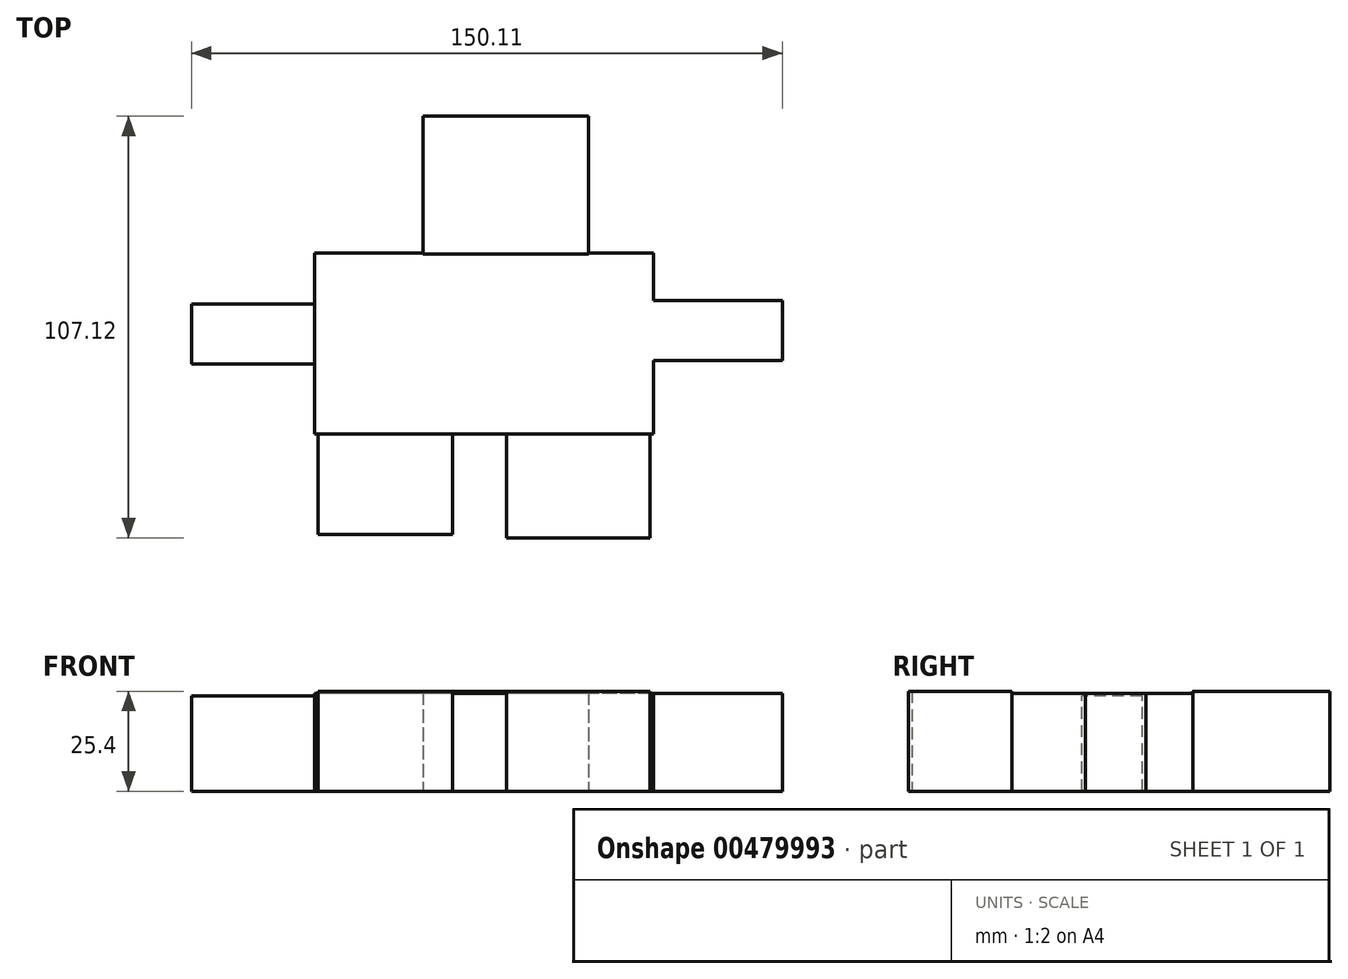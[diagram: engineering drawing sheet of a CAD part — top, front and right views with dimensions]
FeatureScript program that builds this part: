
annotation { "Feature Type Name" : "Feature", "Feature Type Description" : "" }
export const myFeature = defineFeature(function(context is Context, id is Id, definition is map)
    precondition{}
    {
        {
            var Q0;
            Q0=qCreatedBy(makeId("Top.planeOp"),FACE);
            var sketch = newSketch(context, id + "F0", { "sketchPlane" : qUnion([Q0])});
            skLineSegment(sketch, "E0.bottom", {"start": v(-55.67, -25.5) * mm, "end": v(-21.57, -25.5) * mm});
            skLineSegment(sketch, "E0.top", {"start": v(-55.67, 0) * mm, "end": v(-21.57, 0) * mm});
            skLineSegment(sketch, "E0.left", {"start": v(-55.67, -25.5) * mm, "end": v(-55.67, 0) * mm});
            skLineSegment(sketch, "E0.right", {"start": v(-21.57, -25.5) * mm, "end": v(-21.57, 0) * mm});
            skLineSegment(sketch, "E1.bottom", {"start": v(-7.87, -26.38) * mm, "end": v(28.56, -26.38) * mm});
            skLineSegment(sketch, "E1.top", {"start": v(-7.87, 0) * mm, "end": v(28.56, 0) * mm});
            skLineSegment(sketch, "E1.left", {"start": v(-7.87, -26.38) * mm, "end": v(-7.87, 0) * mm});
            skLineSegment(sketch, "E1.right", {"start": v(28.56, -26.38) * mm, "end": v(28.56, 0) * mm});
            skSolve(sketch);
        }
        {
            var Q0;
            Q0 = qSketchRegion(id + "F0", true);
            extrude(context, id + "F1", {"entities" : qUnion([Q0]), "depth" : 25.4 * mm});
        }
        {
            var Q0;
            Q0=qCreatedBy(makeId("Front.planeOp"),FACE);
            var sketch = newSketch(context, id + "F2", { "sketchPlane" : qUnion([Q0])});
            skLineSegment(sketch, "E2.bottom", {"start": v(29.44, 0) * mm, "end": v(-56.55, 0) * mm});
            skLineSegment(sketch, "E2.top", {"start": v(29.44, 24.92) * mm, "end": v(-56.55, 24.92) * mm});
            skLineSegment(sketch, "E2.left", {"start": v(29.44, 0) * mm, "end": v(29.44, 24.92) * mm});
            skLineSegment(sketch, "E2.right", {"start": v(-56.55, 0) * mm, "end": v(-56.55, 24.92) * mm});
            skSolve(sketch);
        }
        {
            var Q0;
            Q0 = qSketchRegion(id + "F2", true);
            extrude(context, id + "F3", {"entities" : qUnion([Q0]), "oppositeDirection" : true, "depth" : 45.97 * mm});
        }
        {
            var Q0;
            Q0=qCreatedBy(makeId("Top.planeOp"),FACE);
            var sketch = newSketch(context, id + "F4", { "sketchPlane" : qUnion([Q0])});
            skLineSegment(sketch, "E3.bottom", {"start": v(-29, 45.76) * mm, "end": v(12.97, 45.76) * mm});
            skLineSegment(sketch, "E3.top", {"start": v(-29, 80.74) * mm, "end": v(12.97, 80.74) * mm});
            skLineSegment(sketch, "E3.left", {"start": v(-29, 45.76) * mm, "end": v(-29, 80.74) * mm});
            skLineSegment(sketch, "E3.right", {"start": v(12.97, 45.76) * mm, "end": v(12.97, 80.74) * mm});
            skSolve(sketch);
        }
        {
            var Q0;
            Q0 = qSketchRegion(id + "F4", true);
            extrude(context, id + "F5", {"entities" : qUnion([Q0]), "operationType" : NewBodyOperationType.ADD, "depth" : 25.4 * mm});
        }
        {
            var Q0;
            Q0=qCreatedBy(makeId("Right.planeOp"),FACE);
            var sketch = newSketch(context, id + "F6", { "sketchPlane" : qUnion([Q0])});
            skLineSegment(sketch, "E4.bottom", {"start": v(33.94, 0) * mm, "end": v(18.63, 0) * mm});
            skLineSegment(sketch, "E4.top", {"start": v(33.94, 24.91) * mm, "end": v(18.63, 24.91) * mm});
            skLineSegment(sketch, "E4.left", {"start": v(33.94, 0) * mm, "end": v(33.94, 24.91) * mm});
            skLineSegment(sketch, "E4.right", {"start": v(18.63, 0) * mm, "end": v(18.63, 24.91) * mm});
            skSolve(sketch);
        }
        {
            var Q0;
            Q0 = qSketchRegion(id + "F6", true);
            extrude(context, id + "F7", {"entities" : qUnion([Q0]), "operationType" : NewBodyOperationType.ADD, "depth" : 62.23 * mm});
        }
        {
            var Q0;
            Q0=qCreatedBy(makeId("Right.planeOp"),FACE);
            var sketch = newSketch(context, id + "F8", { "sketchPlane" : qUnion([Q0])});
            skLineSegment(sketch, "E5.bottom", {"start": v(33.04, 0) * mm, "end": v(17.73, 0) * mm});
            skLineSegment(sketch, "E5.top", {"start": v(33.04, 24.2) * mm, "end": v(17.73, 24.2) * mm});
            skLineSegment(sketch, "E5.left", {"start": v(33.04, 0) * mm, "end": v(33.04, 24.2) * mm});
            skLineSegment(sketch, "E5.right", {"start": v(17.73, 0) * mm, "end": v(17.73, 24.2) * mm});
            skSolve(sketch);
        }
        {
            var Q0;
            Q0 = qSketchRegion(id + "F8", true);
            extrude(context, id + "F9", {"entities" : qUnion([Q0]), "operationType" : NewBodyOperationType.ADD, "oppositeDirection" : true, "depth" : 87.88 * mm});
        }
    });
